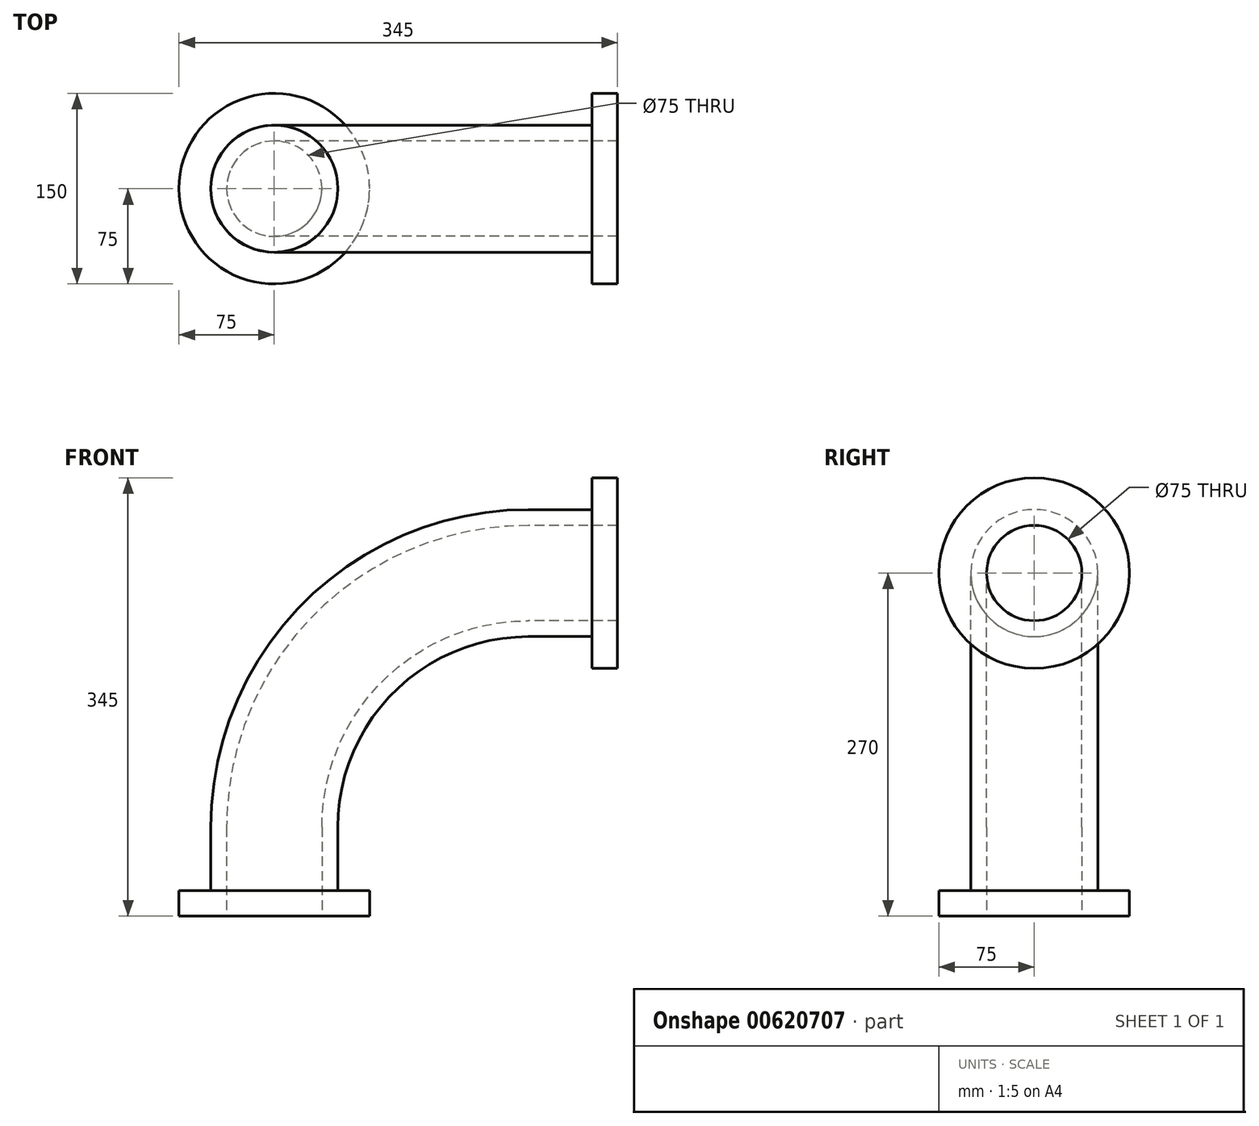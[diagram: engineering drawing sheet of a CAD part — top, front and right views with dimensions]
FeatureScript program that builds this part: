
annotation { "Feature Type Name" : "Feature", "Feature Type Description" : "" }
export const myFeature = defineFeature(function(context is Context, id is Id, definition is map)
    precondition{}
    {
        {
            var Q0;
            Q0=qCreatedBy(makeId("Top.planeOp"),FACE);
            var sketch = newSketch(context, id + "F0", { "sketchPlane" : qUnion([Q0])});
            skCircle(sketch, "E0", {"center": v(0, 0) * mm, "radius": 50 * mm});
            skCircle(sketch, "E1", {"center": v(0, 0) * mm, "radius": 37.5 * mm});
            skCircle(sketch, "E2", {"center": v(0, 0) * mm, "radius": 75 * mm});
            skSolve(sketch);
        }
        {
            var Q0;
            Q0=makeQuery(id+"F0.imprint","IMPRINT",FACE,{"disambiguationData":[TD([[makeQuery(id+"F0.imprint","IMPRINT",EDGE,{"derivedFrom":sQuery(id+"F0.wireOp",EDGE,"E0")}),1.0]])]});
            var Q1;
            Q1=makeQuery(id+"F0.imprint","IMPRINT",FACE,{"disambiguationData":[TD([[makeQuery(id+"F0.imprint","IMPRINT",EDGE,{"derivedFrom":sQuery(id+"F0.wireOp",EDGE,"E0")}),-1.0]])]});
            extrude(context, id + "F1", {"entities" : qUnion([Q0, Q1]), "depth" : 20 * mm, "offsetDistance" : 25 * mm});
        }
        {
            var Q0;
            Q0=makeQuery(id+"F0.imprint","IMPRINT",FACE,{"disambiguationData":[TD([[makeQuery(id+"F0.imprint","IMPRINT",EDGE,{"derivedFrom":sQuery(id+"F0.wireOp",EDGE,"E0")}),1.0]])]});
            extrude(context, id + "F2", {"entities" : qUnion([Q0]), "operationType" : NewBodyOperationType.ADD, "depth" : 70 * mm, "offsetDistance" : 25 * mm});
        }
        {
            var Q0;
            Q0=qCreatedBy(makeId("Front.planeOp"),FACE);
            var sketch = newSketch(context, id + "F3", { "sketchPlane" : qUnion([Q0])});
            skLineSegment(sketch, "E3", {"start": v(0, 0) * mm, "end": v(0, 70) * mm});
            skLineSegment(sketch, "E4", {"start": v(0, 70) * mm, "end": v(200, 70) * mm});
            skArc(sketch, "E5", {"start": v(0, 70) * mm, "mid": v(58.58, 211.42) * mm, "end": v(200, 270) * mm});
            skSolve(sketch);
        }
        {
            var Q0;
            Q0=makeQuery(id+"F2.opExtrude","CAP_FACE",FACE,{"disambiguationData":[OSD([sQuery(id+"F0.wireOp",EDGE,"E0"),sQuery(id+"F0.wireOp",EDGE,"E1")])],"isStart":false});
            var Q1;
            Q1=sQuery(id+"F3.wireOp",EDGE,"E5");
            sweep(context, id + "F4", {"operationType" : NewBodyOperationType.ADD, "profiles" : qUnion([Q0]), "path" : qUnion([Q1])});
        }
        {
            var Q0;
            Q0=makeQuery(id+"F4.opSweep","CAP_FACE",FACE,{"disambiguationData":[OSD([sQuery(id+"F0.wireOp",EDGE,"E0"),sQuery(id+"F0.wireOp",EDGE,"E1"),sQuery(id+"F3.wireOp",VERTEX,"E5.end")])],"isStart":false});
            extrude(context, id + "F5", {"entities" : qUnion([Q0]), "operationType" : NewBodyOperationType.ADD, "depth" : 50 * mm, "offsetDistance" : 25 * mm});
        }
        {
            var Q0;
            Q0=makeQuery(id+"F5.opExtrude","CAP_FACE",FACE,{"disambiguationData":[OSD([sQuery(id+"F0.wireOp",EDGE,"E0"),sQuery(id+"F0.wireOp",EDGE,"E1"),sQuery(id+"F3.wireOp",VERTEX,"E5.end")])],"isStart":false});
            var sketch = newSketch(context, id + "F6", { "sketchPlane" : qUnion([Q0])});
            skCircle(sketch, "E6", {"center": v(0, 270) * mm, "radius": 37.5 * mm});
            skCircle(sketch, "E7", {"center": v(0, 270) * mm, "radius": 75 * mm});
            skSolve(sketch);
        }
        {
            var Q0;
            Q0 = qSketchRegion(id + "F6", true);
            extrude(context, id + "F7", {"entities" : qUnion([Q0]), "operationType" : NewBodyOperationType.ADD, "depth" : 20 * mm, "offsetDistance" : 25 * mm});
        }
    });
